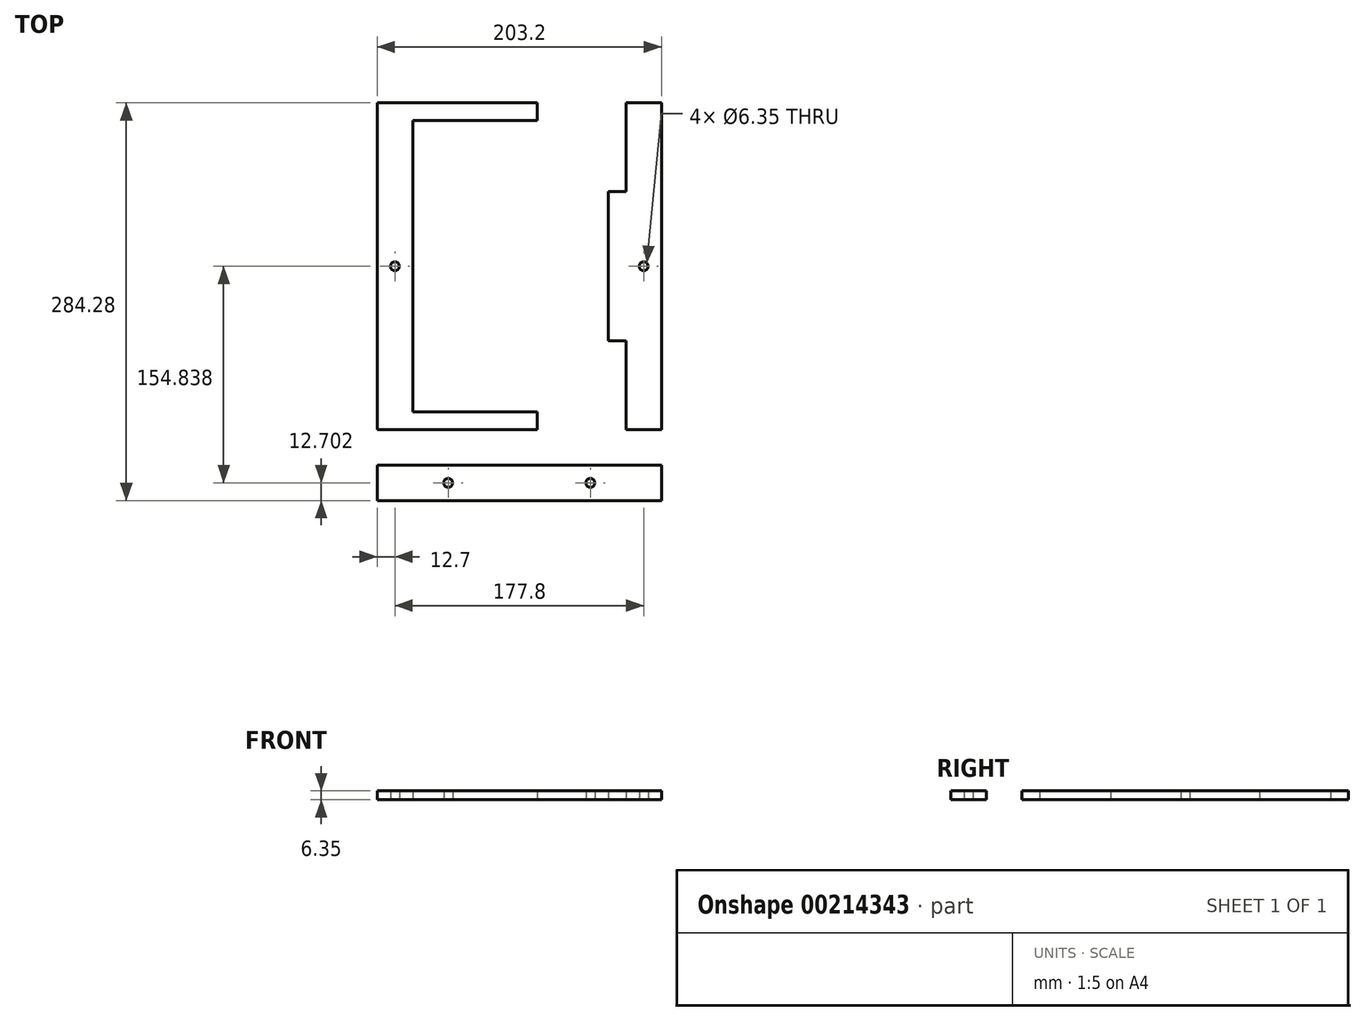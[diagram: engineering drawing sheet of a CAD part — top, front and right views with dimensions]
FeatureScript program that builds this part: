
annotation { "Feature Type Name" : "Feature", "Feature Type Description" : "" }
export const myFeature = defineFeature(function(context is Context, id is Id, definition is map)
    precondition{}
    {
        {
            var Q0;
            Q0=qCreatedBy(makeId("Top.planeOp"),FACE);
            var sketch = newSketch(context, id + "F0", { "sketchPlane" : qUnion([Q0])});
            skLineSegment(sketch, "E0.bottom", {"start": v(76.2, -91.34) * mm, "end": v(-76.2, -91.34) * mm});
            skLineSegment(sketch, "E0.top", {"start": v(76.2, 91.34) * mm, "end": v(-76.2, 91.34) * mm});
            skLineSegment(sketch, "E0.left", {"start": v(76.2, -91.34) * mm, "end": v(76.2, 91.34) * mm});
            skLineSegment(sketch, "E0.right", {"start": v(-76.2, -91.34) * mm, "end": v(-76.2, 91.34) * mm});
            skPoint(sketch, "E0.middle", {"position": v(0, 0) * mm});
            skLineSegment(sketch, "E1.0", {"start": v(101.6, 116.74) * mm, "end": v(-101.6, 116.74) * mm});
            skLineSegment(sketch, "E1.1", {"start": v(101.6, -116.74) * mm, "end": v(101.6, 116.74) * mm});
            skLineSegment(sketch, "E1.2", {"start": v(101.6, -116.74) * mm, "end": v(-101.6, -116.74) * mm});
            skLineSegment(sketch, "E1.3", {"start": v(-101.6, -116.74) * mm, "end": v(-101.6, 116.74) * mm});
            skLineSegment(sketch, "E2.bottom", {"start": v(-101.6, 116.74) * mm, "end": v(101.6, 116.74) * mm});
            skLineSegment(sketch, "E2.top", {"start": v(-101.6, 142.14) * mm, "end": v(101.6, 142.14) * mm});
            skLineSegment(sketch, "E2.left", {"start": v(-101.6, 116.74) * mm, "end": v(-101.6, 142.14) * mm});
            skLineSegment(sketch, "E2.right", {"start": v(101.6, 116.74) * mm, "end": v(101.6, 142.14) * mm});
            skLineSegment(sketch, "E3.bottom", {"start": v(-101.6, -116.74) * mm, "end": v(101.6, -116.74) * mm});
            skLineSegment(sketch, "E3.top", {"start": v(-101.6, -142.14) * mm, "end": v(101.6, -142.14) * mm});
            skLineSegment(sketch, "E3.left", {"start": v(-101.6, -116.74) * mm, "end": v(-101.6, -142.14) * mm});
            skLineSegment(sketch, "E3.right", {"start": v(101.6, -116.74) * mm, "end": v(101.6, -142.14) * mm});
            skLineSegment(sketch, "E4.bottom", {"start": v(76.2, 91.34) * mm, "end": v(63.5, 91.34) * mm});
            skLineSegment(sketch, "E4.top", {"start": v(76.2, 104.04) * mm, "end": v(63.5, 104.04) * mm});
            skLineSegment(sketch, "E4.left", {"start": v(76.2, 91.34) * mm, "end": v(76.2, 104.04) * mm});
            skLineSegment(sketch, "E4.right", {"start": v(63.5, 91.34) * mm, "end": v(63.5, 104.04) * mm});
            skLineSegment(sketch, "E5.bottom", {"start": v(76.2, -91.34) * mm, "end": v(63.5, -91.34) * mm});
            skLineSegment(sketch, "E5.top", {"start": v(76.2, -104.04) * mm, "end": v(63.5, -104.04) * mm});
            skLineSegment(sketch, "E5.left", {"start": v(76.2, -91.34) * mm, "end": v(76.2, -104.04) * mm});
            skLineSegment(sketch, "E5.right", {"start": v(63.5, -91.34) * mm, "end": v(63.5, -104.04) * mm});
            skLineSegment(sketch, "E6", {"start": v(76.2, -104.04) * mm, "end": v(88.9, -104.04) * mm});
            skLineSegment(sketch, "E7", {"start": v(88.9, -104.04) * mm, "end": v(88.9, -53.24) * mm});
            skLineSegment(sketch, "E8", {"start": v(88.9, -53.24) * mm, "end": v(76.2, -53.24) * mm});
            skLineSegment(sketch, "E9", {"start": v(76.2, 104.04) * mm, "end": v(88.9, 104.04) * mm});
            skLineSegment(sketch, "E10", {"start": v(88.9, 104.04) * mm, "end": v(88.9, 53.24) * mm});
            skLineSegment(sketch, "E11", {"start": v(88.9, 53.24) * mm, "end": v(76.2, 53.24) * mm});
            skLineSegment(sketch, "E12", {"start": v(101.6, 142.14) * mm, "end": v(127, 142.14) * mm});
            skLineSegment(sketch, "E13", {"start": v(127, 142.14) * mm, "end": v(127, -142.14) * mm});
            skLineSegment(sketch, "E14", {"start": v(127, -142.14) * mm, "end": v(101.6, -142.14) * mm});
            skLineSegment(sketch, "E15", {"start": v(76.2, -53.24) * mm, "end": v(63.5, -53.24) * mm});
            skLineSegment(sketch, "E16", {"start": v(63.5, -53.24) * mm, "end": v(63.5, 53.24) * mm});
            skLineSegment(sketch, "E17", {"start": v(63.5, 53.24) * mm, "end": v(76.2, 53.24) * mm});
            skLineSegment(sketch, "E18", {"start": v(63.5, 104.04) * mm, "end": v(50.8, 104.04) * mm});
            skLineSegment(sketch, "E19", {"start": v(50.8, 104.04) * mm, "end": v(50.8, 91.34) * mm});
            skLineSegment(sketch, "E20", {"start": v(63.5, -104.04) * mm, "end": v(50.8, -104.04) * mm});
            skLineSegment(sketch, "E21", {"start": v(50.8, -104.04) * mm, "end": v(50.8, -91.34) * mm});
            skLineSegment(sketch, "E22", {"start": v(76.2, -104.04) * mm, "end": v(76.2, -116.74) * mm});
            skLineSegment(sketch, "E23", {"start": v(50.8, -104.04) * mm, "end": v(50.8, -116.74) * mm});
            skLineSegment(sketch, "E24", {"start": v(50.8, -104.04) * mm, "end": v(-76.2, -104.04) * mm});
            skLineSegment(sketch, "E25", {"start": v(-76.2, -104.04) * mm, "end": v(-76.2, -91.34) * mm});
            skLineSegment(sketch, "E26", {"start": v(76.2, 104.04) * mm, "end": v(76.2, 116.74) * mm});
            skLineSegment(sketch, "E27", {"start": v(50.8, 104.04) * mm, "end": v(50.8, 116.74) * mm});
            skLineSegment(sketch, "E28", {"start": v(50.8, 104.04) * mm, "end": v(-76.2, 104.04) * mm});
            skLineSegment(sketch, "E29", {"start": v(-76.2, 104.04) * mm, "end": v(-76.2, 91.34) * mm});
            skLineSegment(sketch, "E30", {"start": v(12.7, -104.04) * mm, "end": v(12.7, -116.74) * mm});
            skLineSegment(sketch, "E31", {"start": v(12.7, 116.74) * mm, "end": v(12.7, 104.04) * mm});
            skLineSegment(sketch, "E32.top", {"start": v(-101.6, -167.54) * mm, "end": v(101.6, -167.54) * mm});
            skLineSegment(sketch, "E32.left", {"start": v(-101.6, -142.14) * mm, "end": v(-101.6, -167.54) * mm});
            skLineSegment(sketch, "E32.right", {"start": v(101.6, -142.14) * mm, "end": v(101.6, -167.54) * mm});
            skCircle(sketch, "E33", {"center": v(-50.8, -154.84) * mm, "radius": 3.18 * mm});
            skPoint(sketch, "E33.centerSnap0", {"position": v(-101.6, -154.84) * mm});
            skCircle(sketch, "E34", {"center": v(50.8, -154.84) * mm, "radius": 3.17 * mm});
            skCircle(sketch, "E35", {"center": v(-88.9, 0) * mm, "radius": 3.18 * mm});
            skCircle(sketch, "E36", {"center": v(88.9, 0) * mm, "radius": 3.18 * mm});
            skCircle(sketch, "E37", {"center": v(-88.9, 129.44) * mm, "radius": 3.17 * mm});
            skPoint(sketch, "E37.centerSnap0", {"position": v(-101.6, 129.44) * mm});
            skCircle(sketch, "E38", {"center": v(0, 129.44) * mm, "radius": 3.18 * mm});
            skCircle(sketch, "E39", {"center": v(88.9, 129.44) * mm, "radius": 3.18 * mm});
            skPoint(sketch, "E39.centerSnap0", {"position": v(101.6, 129.44) * mm});
            skCircle(sketch, "E40", {"center": v(-88.9, -129.44) * mm, "radius": 3.18 * mm});
            skPoint(sketch, "E40.centerSnap0", {"position": v(-101.6, -129.44) * mm});
            skCircle(sketch, "E41", {"center": v(0, -129.44) * mm, "radius": 3.18 * mm});
            skCircle(sketch, "E42", {"center": v(88.9, -129.44) * mm, "radius": 3.18 * mm});
            skPoint(sketch, "E42.centerSnap0", {"position": v(101.6, -129.44) * mm});
            skSolve(sketch);
        }
        {
            var Q0;
            Q0=makeQuery(id+"F0.imprint","IMPRINT",FACE,{"disambiguationData":[TD([[makeQuery(id+"F0.imprint","IMPRINT",EDGE,{"derivedFrom":sQuery(id+"F0.wireOp",EDGE,"E2.bottom")}),1.0]])]});
            var Q1;
            Q1=makeQuery(id+"F0.imprint","IMPRINT",FACE,{"disambiguationData":[TD([[makeQuery(id+"F0.imprint","IMPRINT",EDGE,{"derivedFrom":sQuery(id+"F0.wireOp",EDGE,"E3.bottom")}),-1.0]])]});
            var Q2;
            {var subQ0=sQuery(id+"F0.wireOp",EDGE,"E0.right");Q2=makeQuery(id+"F0.imprint","IMPRINT",FACE,{"disambiguationData":[TD([[makeQuery(id+"F0.imprint","IMPRINT",EDGE,{"derivedFrom":subQ0}),1.0]])]});}
            var Q3;
            {var subQ0=sQuery(id+"F0.wireOp",EDGE,"E5.left");Q3=makeQuery(id+"F0.imprint","IMPRINT",FACE,{"disambiguationData":[TD([[makeQuery(id+"F0.imprint","IMPRINT",EDGE,{"derivedFrom":subQ0}),1.0]])]});}
            var Q4;
            {var subQ0=sQuery(id+"F0.wireOp",EDGE,"E15");Q4=makeQuery(id+"F0.imprint","IMPRINT",FACE,{"disambiguationData":[TD([[makeQuery(id+"F0.imprint","IMPRINT",EDGE,{"derivedFrom":subQ0}),-1.0]])]});}
            var Q5;
            {var subQ0=sQuery(id+"F0.wireOp",EDGE,"E4.left");Q5=makeQuery(id+"F0.imprint","IMPRINT",FACE,{"disambiguationData":[TD([[makeQuery(id+"F0.imprint","IMPRINT",EDGE,{"derivedFrom":subQ0}),-1.0]])]});}
            var Q6;
            {var subQ2=sQuery(id+"F0.wireOp",EDGE,"E1.1");Q6=makeQuery(id+"F0.imprint","IMPRINT",FACE,{"disambiguationData":[TD([[makeQuery(id+"F0.imprint","IMPRINT",EDGE,{"derivedFrom":subQ2}),1.0]])]});}
            var Q7;
            Q7=makeQuery(id+"F0.imprint","IMPRINT",FACE,{"disambiguationData":[TD([[makeQuery(id+"F0.imprint","IMPRINT",EDGE,{"derivedFrom":sQuery(id+"F0.wireOp",EDGE,"E3.top")}),-1.0]])]});
            extrude(context, id + "F1", {"entities" : qUnion([Q0, Q1, Q2, Q3, Q4, Q5, Q6, Q7]), "depth" : 6.35 * mm});
        }
    });
